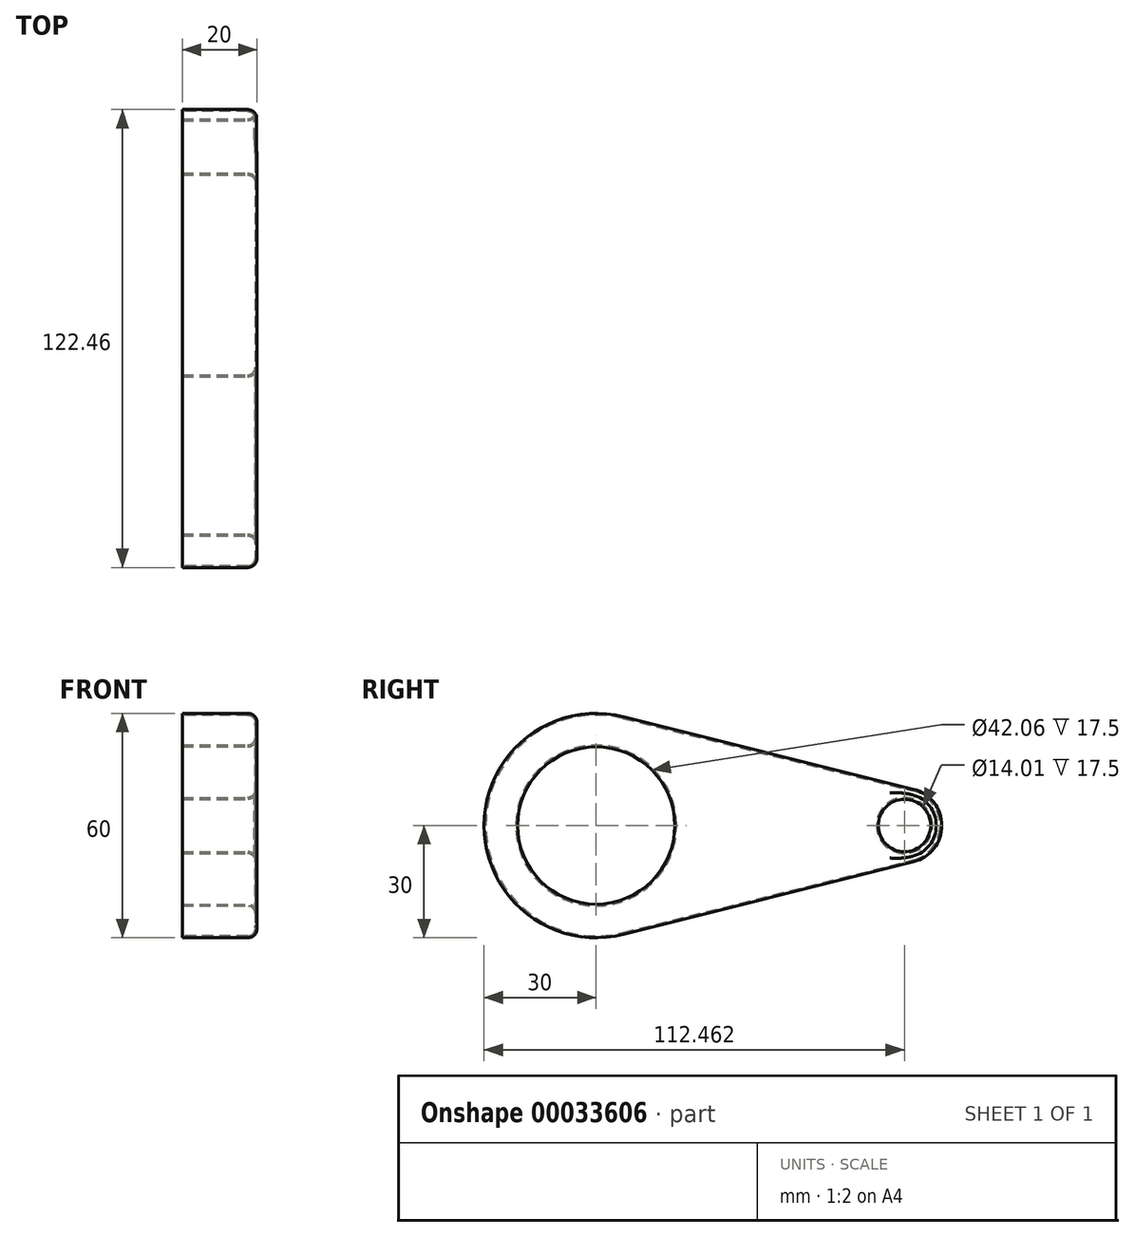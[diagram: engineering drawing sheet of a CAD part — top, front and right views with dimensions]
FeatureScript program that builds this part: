
annotation { "Feature Type Name" : "Feature", "Feature Type Description" : "" }
export const myFeature = defineFeature(function(context is Context, id is Id, definition is map)
    precondition{}
    {
        {
            var Q0;
            Q0=qCreatedBy(makeId("Right.planeOp"),FACE);
            var sketch = newSketch(context, id + "F0", { "sketchPlane" : qUnion([Q0])});
            skCircle(sketch, "E0", {"center": v(0, 0) * mm, "radius": 30 * mm});
            skCircle(sketch, "E1", {"center": v(82.46, 0) * mm, "radius": 10 * mm});
            skLineSegment(sketch, "E2", {"start": v(7.28, 29.1) * mm, "end": v(84.89, 9.7) * mm});
            skLineSegment(sketch, "E3", {"start": v(7.28, -29.1) * mm, "end": v(84.89, -9.7) * mm});
            skSolve(sketch);
        }
        {
            var Q0;
            Q0 = qSketchRegion(id + "F0", true);
            extrude(context, id + "F1", {"entities" : qUnion([Q0]), "depth" : 20 * mm});
        }
        {
            var Q0;
            Q0=makeQuery(id+"F1.opExtrude","CAP_FACE",FACE,{"disambiguationData":[OSD([sQuery(id+"F0.wireOp",EDGE,"E0"),sQuery(id+"F0.wireOp",EDGE,"E1"),sQuery(id+"F0.wireOp",EDGE,"E2"),sQuery(id+"F0.wireOp",EDGE,"E3")])],"isStart":false});
            var sketch = newSketch(context, id + "F2", { "sketchPlane" : qUnion([Q0])});
            skCircle(sketch, "E4", {"center": v(0, 0) * mm, "radius": 21.03 * mm});
            skCircle(sketch, "E5", {"center": v(82.46, 0) * mm, "radius": 7 * mm});
            skSolve(sketch);
        }
        {
            var Q0;
            Q0=makeQuery(id+"F2.imprint","IMPRINT",FACE,{"disambiguationData":[TD([[makeQuery(id+"F2.imprint","IMPRINT",EDGE,{"derivedFrom":sQuery(id+"F2.wireOp",EDGE,"E5")}),1.0]])]});
            var Q1;
            Q1=makeQuery(id+"F2.imprint","IMPRINT",FACE,{"disambiguationData":[TD([[makeQuery(id+"F2.imprint","IMPRINT",EDGE,{"derivedFrom":sQuery(id+"F2.wireOp",EDGE,"E4")}),1.0]])]});
            extrude(context, id + "F3", {"entities" : qUnion([Q0, Q1]), "operationType" : NewBodyOperationType.REMOVE, "oppositeDirection" : true, "depth" : 20 * mm});
        }
        {
            var Q0;
            Q0=makeQuery(id+"F1.opExtrude","CAP_FACE",FACE,{"disambiguationData":[OSD([sQuery(id+"F0.wireOp",EDGE,"E0"),sQuery(id+"F0.wireOp",EDGE,"E1"),sQuery(id+"F0.wireOp",EDGE,"E2"),sQuery(id+"F0.wireOp",EDGE,"E3")])],"isStart":false});
            var Q1;
            Q1=makeQuery(id+"F3.boolean.opBoolean","COPY",FACE,{"derivedFrom":makeQuery(id+"F3.opExtrude","CAP_FACE",FACE,{"disambiguationData":[OSD([sQuery(id+"F2.wireOp",EDGE,"E4")])],"isStart":false})});
            var Q2;
            Q2=makeQuery(id+"F3.boolean.opBoolean","COPY",FACE,{"derivedFrom":makeQuery(id+"F3.opExtrude","CAP_FACE",FACE,{"disambiguationData":[OSD([sQuery(id+"F2.wireOp",EDGE,"E5")])],"isStart":false})});
            fillet(context, id + "F4", {"entities" : qUnion([Q0, Q1, Q2]), "radius" : 2.5 * mm, "tangentPropagation" : true, "allowEdgeOverflow" : false});
        }
        {
            var Q0;
            Q0=makeQuery(id+"F1.opExtrude","CAP_FACE",FACE,{"disambiguationData":[OSD([sQuery(id+"F0.wireOp",EDGE,"E0"),sQuery(id+"F0.wireOp",EDGE,"E1"),sQuery(id+"F0.wireOp",EDGE,"E2"),sQuery(id+"F0.wireOp",EDGE,"E3")])],"isStart":true});
            shell(context, id + "F5", {"entities" : qUnion([Q0]), "thickness" : 0.5 * mm});
        }
    });
